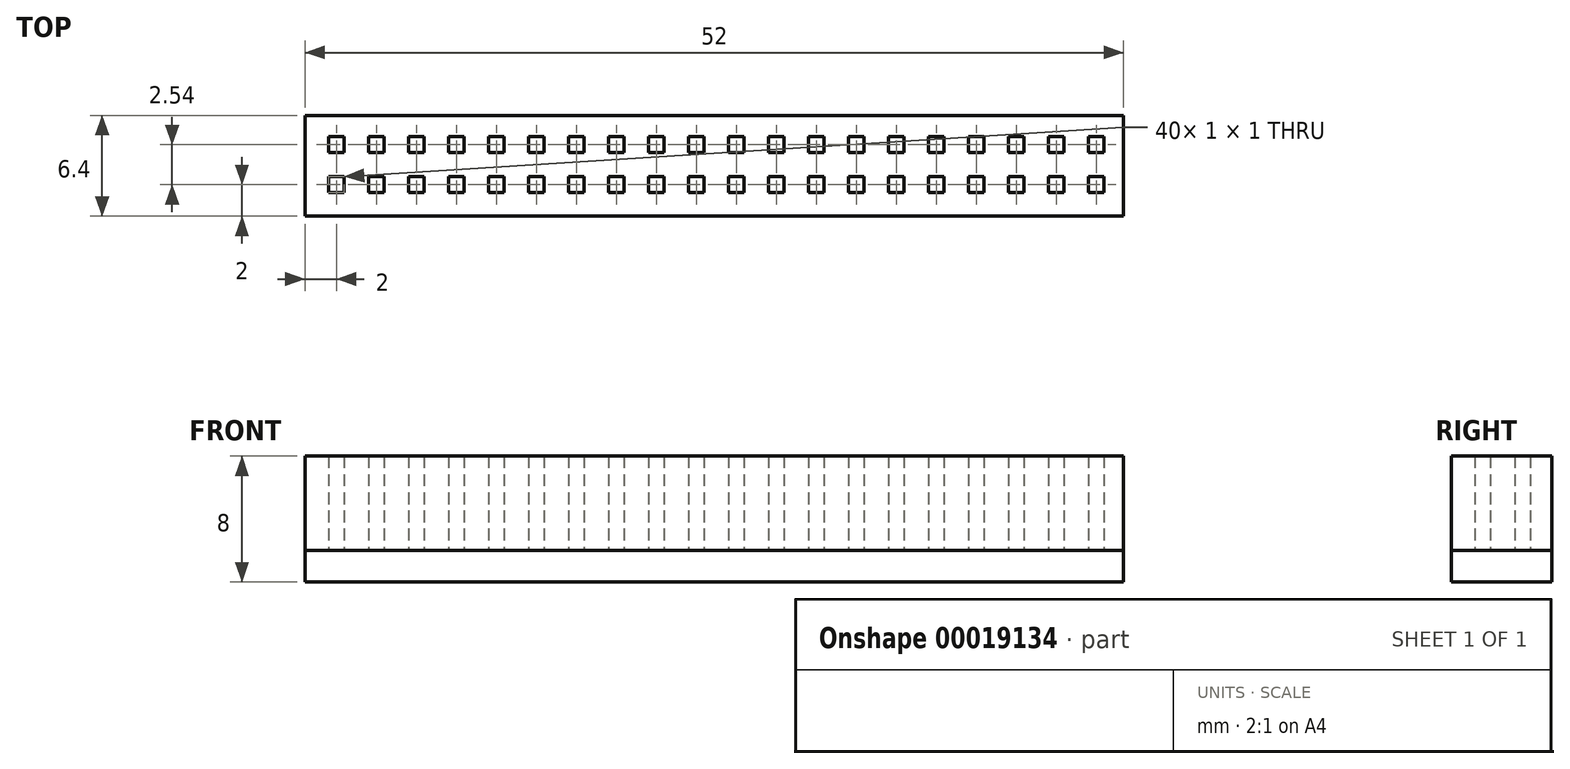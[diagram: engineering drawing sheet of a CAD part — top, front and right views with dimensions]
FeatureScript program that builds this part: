
annotation { "Feature Type Name" : "Feature", "Feature Type Description" : "" }
export const myFeature = defineFeature(function(context is Context, id is Id, definition is map)
    precondition{}
    {
        {
            var Q0;
            Q0=qCreatedBy(makeId("Top.planeOp"),FACE);
            var sketch = newSketch(context, id + "F0", { "sketchPlane" : qUnion([Q0])});
            skLineSegment(sketch, "E0.bottom", {"start": v(0, 0) * mm, "end": v(52, 0) * mm});
            skLineSegment(sketch, "E0.top", {"start": v(0, 6.4) * mm, "end": v(52, 6.4) * mm});
            skLineSegment(sketch, "E0.left", {"start": v(0, 0) * mm, "end": v(0, 6.4) * mm});
            skLineSegment(sketch, "E0.right", {"start": v(52, 0) * mm, "end": v(52, 6.4) * mm});
            skLineSegment(sketch, "E1.bottom", {"start": v(1.5, 1.5) * mm, "end": v(2.5, 1.5) * mm});
            skLineSegment(sketch, "E1.top", {"start": v(1.5, 2.5) * mm, "end": v(2.5, 2.5) * mm});
            skLineSegment(sketch, "E1.left", {"start": v(1.5, 1.5) * mm, "end": v(1.5, 2.5) * mm});
            skLineSegment(sketch, "E1.right", {"start": v(2.5, 1.5) * mm, "end": v(2.5, 2.5) * mm});
            skLineSegment(sketch, "E2.0.1.0", {"start": v(2.5, 4.04) * mm, "end": v(2.5, 5.04) * mm});
            skLineSegment(sketch, "E2.0.1.1", {"start": v(1.5, 4.04) * mm, "end": v(1.5, 5.04) * mm});
            skLineSegment(sketch, "E2.0.1.2", {"start": v(1.5, 5.04) * mm, "end": v(2.5, 5.04) * mm});
            skLineSegment(sketch, "E2.0.1.3", {"start": v(1.5, 4.04) * mm, "end": v(2.5, 4.04) * mm});
            skLineSegment(sketch, "E2.1.0.0", {"start": v(5.04, 1.5) * mm, "end": v(5.04, 2.5) * mm});
            skLineSegment(sketch, "E2.1.0.1", {"start": v(4.04, 1.5) * mm, "end": v(4.04, 2.5) * mm});
            skLineSegment(sketch, "E2.1.0.2", {"start": v(4.04, 2.5) * mm, "end": v(5.04, 2.5) * mm});
            skLineSegment(sketch, "E2.1.0.3", {"start": v(4.04, 1.5) * mm, "end": v(5.04, 1.5) * mm});
            skLineSegment(sketch, "E2.1.1.0", {"start": v(5.04, 4.04) * mm, "end": v(5.04, 5.04) * mm});
            skLineSegment(sketch, "E2.1.1.1", {"start": v(4.04, 4.04) * mm, "end": v(4.04, 5.04) * mm});
            skLineSegment(sketch, "E2.1.1.2", {"start": v(4.04, 5.04) * mm, "end": v(5.04, 5.04) * mm});
            skLineSegment(sketch, "E2.1.1.3", {"start": v(4.04, 4.04) * mm, "end": v(5.04, 4.04) * mm});
            skLineSegment(sketch, "E2.2.0.0", {"start": v(7.58, 1.5) * mm, "end": v(7.58, 2.5) * mm});
            skLineSegment(sketch, "E2.2.0.1", {"start": v(6.58, 1.5) * mm, "end": v(6.58, 2.5) * mm});
            skLineSegment(sketch, "E2.2.0.2", {"start": v(6.58, 2.5) * mm, "end": v(7.58, 2.5) * mm});
            skLineSegment(sketch, "E2.2.0.3", {"start": v(6.58, 1.5) * mm, "end": v(7.58, 1.5) * mm});
            skLineSegment(sketch, "E2.2.1.0", {"start": v(7.58, 4.04) * mm, "end": v(7.58, 5.04) * mm});
            skLineSegment(sketch, "E2.2.1.1", {"start": v(6.58, 4.04) * mm, "end": v(6.58, 5.04) * mm});
            skLineSegment(sketch, "E2.2.1.2", {"start": v(6.58, 5.04) * mm, "end": v(7.58, 5.04) * mm});
            skLineSegment(sketch, "E2.2.1.3", {"start": v(6.58, 4.04) * mm, "end": v(7.58, 4.04) * mm});
            skLineSegment(sketch, "E2.3.0.0", {"start": v(10.12, 1.5) * mm, "end": v(10.12, 2.5) * mm});
            skLineSegment(sketch, "E2.3.0.1", {"start": v(9.12, 1.5) * mm, "end": v(9.12, 2.5) * mm});
            skLineSegment(sketch, "E2.3.0.2", {"start": v(9.12, 2.5) * mm, "end": v(10.12, 2.5) * mm});
            skLineSegment(sketch, "E2.3.0.3", {"start": v(9.12, 1.5) * mm, "end": v(10.12, 1.5) * mm});
            skLineSegment(sketch, "E2.3.1.0", {"start": v(10.12, 4.04) * mm, "end": v(10.12, 5.04) * mm});
            skLineSegment(sketch, "E2.3.1.1", {"start": v(9.12, 4.04) * mm, "end": v(9.12, 5.04) * mm});
            skLineSegment(sketch, "E2.3.1.2", {"start": v(9.12, 5.04) * mm, "end": v(10.12, 5.04) * mm});
            skLineSegment(sketch, "E2.3.1.3", {"start": v(9.12, 4.04) * mm, "end": v(10.12, 4.04) * mm});
            skLineSegment(sketch, "E2.4.0.0", {"start": v(12.66, 1.5) * mm, "end": v(12.66, 2.5) * mm});
            skLineSegment(sketch, "E2.4.0.1", {"start": v(11.66, 1.5) * mm, "end": v(11.66, 2.5) * mm});
            skLineSegment(sketch, "E2.4.0.2", {"start": v(11.66, 2.5) * mm, "end": v(12.66, 2.5) * mm});
            skLineSegment(sketch, "E2.4.0.3", {"start": v(11.66, 1.5) * mm, "end": v(12.66, 1.5) * mm});
            skLineSegment(sketch, "E2.4.1.0", {"start": v(12.66, 4.04) * mm, "end": v(12.66, 5.04) * mm});
            skLineSegment(sketch, "E2.4.1.1", {"start": v(11.66, 4.04) * mm, "end": v(11.66, 5.04) * mm});
            skLineSegment(sketch, "E2.4.1.2", {"start": v(11.66, 5.04) * mm, "end": v(12.66, 5.04) * mm});
            skLineSegment(sketch, "E2.4.1.3", {"start": v(11.66, 4.04) * mm, "end": v(12.66, 4.04) * mm});
            skLineSegment(sketch, "E2.5.0.0", {"start": v(15.2, 1.5) * mm, "end": v(15.2, 2.5) * mm});
            skLineSegment(sketch, "E2.5.0.1", {"start": v(14.2, 1.5) * mm, "end": v(14.2, 2.5) * mm});
            skLineSegment(sketch, "E2.5.0.2", {"start": v(14.2, 2.5) * mm, "end": v(15.2, 2.5) * mm});
            skLineSegment(sketch, "E2.5.0.3", {"start": v(14.2, 1.5) * mm, "end": v(15.2, 1.5) * mm});
            skLineSegment(sketch, "E2.5.1.0", {"start": v(15.2, 4.04) * mm, "end": v(15.2, 5.04) * mm});
            skLineSegment(sketch, "E2.5.1.1", {"start": v(14.2, 4.04) * mm, "end": v(14.2, 5.04) * mm});
            skLineSegment(sketch, "E2.5.1.2", {"start": v(14.2, 5.04) * mm, "end": v(15.2, 5.04) * mm});
            skLineSegment(sketch, "E2.5.1.3", {"start": v(14.2, 4.04) * mm, "end": v(15.2, 4.04) * mm});
            skLineSegment(sketch, "E2.6.0.0", {"start": v(17.74, 1.5) * mm, "end": v(17.74, 2.5) * mm});
            skLineSegment(sketch, "E2.6.0.1", {"start": v(16.74, 1.5) * mm, "end": v(16.74, 2.5) * mm});
            skLineSegment(sketch, "E2.6.0.2", {"start": v(16.74, 2.5) * mm, "end": v(17.74, 2.5) * mm});
            skLineSegment(sketch, "E2.6.0.3", {"start": v(16.74, 1.5) * mm, "end": v(17.74, 1.5) * mm});
            skLineSegment(sketch, "E2.6.1.0", {"start": v(17.74, 4.04) * mm, "end": v(17.74, 5.04) * mm});
            skLineSegment(sketch, "E2.6.1.1", {"start": v(16.74, 4.04) * mm, "end": v(16.74, 5.04) * mm});
            skLineSegment(sketch, "E2.6.1.2", {"start": v(16.74, 5.04) * mm, "end": v(17.74, 5.04) * mm});
            skLineSegment(sketch, "E2.6.1.3", {"start": v(16.74, 4.04) * mm, "end": v(17.74, 4.04) * mm});
            skLineSegment(sketch, "E2.7.0.0", {"start": v(20.28, 1.5) * mm, "end": v(20.28, 2.5) * mm});
            skLineSegment(sketch, "E2.7.0.1", {"start": v(19.28, 1.5) * mm, "end": v(19.28, 2.5) * mm});
            skLineSegment(sketch, "E2.7.0.2", {"start": v(19.28, 2.5) * mm, "end": v(20.28, 2.5) * mm});
            skLineSegment(sketch, "E2.7.0.3", {"start": v(19.28, 1.5) * mm, "end": v(20.28, 1.5) * mm});
            skLineSegment(sketch, "E2.7.1.0", {"start": v(20.28, 4.04) * mm, "end": v(20.28, 5.04) * mm});
            skLineSegment(sketch, "E2.7.1.1", {"start": v(19.28, 4.04) * mm, "end": v(19.28, 5.04) * mm});
            skLineSegment(sketch, "E2.7.1.2", {"start": v(19.28, 5.04) * mm, "end": v(20.28, 5.04) * mm});
            skLineSegment(sketch, "E2.7.1.3", {"start": v(19.28, 4.04) * mm, "end": v(20.28, 4.04) * mm});
            skLineSegment(sketch, "E2.8.0.0", {"start": v(22.82, 1.5) * mm, "end": v(22.82, 2.5) * mm});
            skLineSegment(sketch, "E2.8.0.1", {"start": v(21.82, 1.5) * mm, "end": v(21.82, 2.5) * mm});
            skLineSegment(sketch, "E2.8.0.2", {"start": v(21.82, 2.5) * mm, "end": v(22.82, 2.5) * mm});
            skLineSegment(sketch, "E2.8.0.3", {"start": v(21.82, 1.5) * mm, "end": v(22.82, 1.5) * mm});
            skLineSegment(sketch, "E2.8.1.0", {"start": v(22.82, 4.04) * mm, "end": v(22.82, 5.04) * mm});
            skLineSegment(sketch, "E2.8.1.1", {"start": v(21.82, 4.04) * mm, "end": v(21.82, 5.04) * mm});
            skLineSegment(sketch, "E2.8.1.2", {"start": v(21.82, 5.04) * mm, "end": v(22.82, 5.04) * mm});
            skLineSegment(sketch, "E2.8.1.3", {"start": v(21.82, 4.04) * mm, "end": v(22.82, 4.04) * mm});
            skLineSegment(sketch, "E2.9.0.0", {"start": v(25.36, 1.5) * mm, "end": v(25.36, 2.5) * mm});
            skLineSegment(sketch, "E2.9.0.1", {"start": v(24.36, 1.5) * mm, "end": v(24.36, 2.5) * mm});
            skLineSegment(sketch, "E2.9.0.2", {"start": v(24.36, 2.5) * mm, "end": v(25.36, 2.5) * mm});
            skLineSegment(sketch, "E2.9.0.3", {"start": v(24.36, 1.5) * mm, "end": v(25.36, 1.5) * mm});
            skLineSegment(sketch, "E2.9.1.0", {"start": v(25.36, 4.04) * mm, "end": v(25.36, 5.04) * mm});
            skLineSegment(sketch, "E2.9.1.1", {"start": v(24.36, 4.04) * mm, "end": v(24.36, 5.04) * mm});
            skLineSegment(sketch, "E2.9.1.2", {"start": v(24.36, 5.04) * mm, "end": v(25.36, 5.04) * mm});
            skLineSegment(sketch, "E2.9.1.3", {"start": v(24.36, 4.04) * mm, "end": v(25.36, 4.04) * mm});
            skLineSegment(sketch, "E2.10.0.0", {"start": v(27.9, 1.5) * mm, "end": v(27.9, 2.5) * mm});
            skLineSegment(sketch, "E2.10.0.1", {"start": v(26.9, 1.5) * mm, "end": v(26.9, 2.5) * mm});
            skLineSegment(sketch, "E2.10.0.2", {"start": v(26.9, 2.5) * mm, "end": v(27.9, 2.5) * mm});
            skLineSegment(sketch, "E2.10.0.3", {"start": v(26.9, 1.5) * mm, "end": v(27.9, 1.5) * mm});
            skLineSegment(sketch, "E2.10.1.0", {"start": v(27.9, 4.04) * mm, "end": v(27.9, 5.04) * mm});
            skLineSegment(sketch, "E2.10.1.1", {"start": v(26.9, 4.04) * mm, "end": v(26.9, 5.04) * mm});
            skLineSegment(sketch, "E2.10.1.2", {"start": v(26.9, 5.04) * mm, "end": v(27.9, 5.04) * mm});
            skLineSegment(sketch, "E2.10.1.3", {"start": v(26.9, 4.04) * mm, "end": v(27.9, 4.04) * mm});
            skLineSegment(sketch, "E2.11.0.0", {"start": v(30.44, 1.5) * mm, "end": v(30.44, 2.5) * mm});
            skLineSegment(sketch, "E2.11.0.1", {"start": v(29.44, 1.5) * mm, "end": v(29.44, 2.5) * mm});
            skLineSegment(sketch, "E2.11.0.2", {"start": v(29.44, 2.5) * mm, "end": v(30.44, 2.5) * mm});
            skLineSegment(sketch, "E2.11.0.3", {"start": v(29.44, 1.5) * mm, "end": v(30.44, 1.5) * mm});
            skLineSegment(sketch, "E2.11.1.0", {"start": v(30.44, 4.04) * mm, "end": v(30.44, 5.04) * mm});
            skLineSegment(sketch, "E2.11.1.1", {"start": v(29.44, 4.04) * mm, "end": v(29.44, 5.04) * mm});
            skLineSegment(sketch, "E2.11.1.2", {"start": v(29.44, 5.04) * mm, "end": v(30.44, 5.04) * mm});
            skLineSegment(sketch, "E2.11.1.3", {"start": v(29.44, 4.04) * mm, "end": v(30.44, 4.04) * mm});
            skLineSegment(sketch, "E2.12.0.0", {"start": v(32.98, 1.5) * mm, "end": v(32.98, 2.5) * mm});
            skLineSegment(sketch, "E2.12.0.1", {"start": v(31.98, 1.5) * mm, "end": v(31.98, 2.5) * mm});
            skLineSegment(sketch, "E2.12.0.2", {"start": v(31.98, 2.5) * mm, "end": v(32.98, 2.5) * mm});
            skLineSegment(sketch, "E2.12.0.3", {"start": v(31.98, 1.5) * mm, "end": v(32.98, 1.5) * mm});
            skLineSegment(sketch, "E2.12.1.0", {"start": v(32.98, 4.04) * mm, "end": v(32.98, 5.04) * mm});
            skLineSegment(sketch, "E2.12.1.1", {"start": v(31.98, 4.04) * mm, "end": v(31.98, 5.04) * mm});
            skLineSegment(sketch, "E2.12.1.2", {"start": v(31.98, 5.04) * mm, "end": v(32.98, 5.04) * mm});
            skLineSegment(sketch, "E2.12.1.3", {"start": v(31.98, 4.04) * mm, "end": v(32.98, 4.04) * mm});
            skLineSegment(sketch, "E2.13.0.0", {"start": v(35.52, 1.5) * mm, "end": v(35.52, 2.5) * mm});
            skLineSegment(sketch, "E2.13.0.1", {"start": v(34.52, 1.5) * mm, "end": v(34.52, 2.5) * mm});
            skLineSegment(sketch, "E2.13.0.2", {"start": v(34.52, 2.5) * mm, "end": v(35.52, 2.5) * mm});
            skLineSegment(sketch, "E2.13.0.3", {"start": v(34.52, 1.5) * mm, "end": v(35.52, 1.5) * mm});
            skLineSegment(sketch, "E2.13.1.0", {"start": v(35.52, 4.04) * mm, "end": v(35.52, 5.04) * mm});
            skLineSegment(sketch, "E2.13.1.1", {"start": v(34.52, 4.04) * mm, "end": v(34.52, 5.04) * mm});
            skLineSegment(sketch, "E2.13.1.2", {"start": v(34.52, 5.04) * mm, "end": v(35.52, 5.04) * mm});
            skLineSegment(sketch, "E2.13.1.3", {"start": v(34.52, 4.04) * mm, "end": v(35.52, 4.04) * mm});
            skLineSegment(sketch, "E2.14.0.0", {"start": v(38.06, 1.5) * mm, "end": v(38.06, 2.5) * mm});
            skLineSegment(sketch, "E2.14.0.1", {"start": v(37.06, 1.5) * mm, "end": v(37.06, 2.5) * mm});
            skLineSegment(sketch, "E2.14.0.2", {"start": v(37.06, 2.5) * mm, "end": v(38.06, 2.5) * mm});
            skLineSegment(sketch, "E2.14.0.3", {"start": v(37.06, 1.5) * mm, "end": v(38.06, 1.5) * mm});
            skLineSegment(sketch, "E2.14.1.0", {"start": v(38.06, 4.04) * mm, "end": v(38.06, 5.04) * mm});
            skLineSegment(sketch, "E2.14.1.1", {"start": v(37.06, 4.04) * mm, "end": v(37.06, 5.04) * mm});
            skLineSegment(sketch, "E2.14.1.2", {"start": v(37.06, 5.04) * mm, "end": v(38.06, 5.04) * mm});
            skLineSegment(sketch, "E2.14.1.3", {"start": v(37.06, 4.04) * mm, "end": v(38.06, 4.04) * mm});
            skLineSegment(sketch, "E2.15.0.0", {"start": v(40.6, 1.5) * mm, "end": v(40.6, 2.5) * mm});
            skLineSegment(sketch, "E2.15.0.1", {"start": v(39.6, 1.5) * mm, "end": v(39.6, 2.5) * mm});
            skLineSegment(sketch, "E2.15.0.2", {"start": v(39.6, 2.5) * mm, "end": v(40.6, 2.5) * mm});
            skLineSegment(sketch, "E2.15.0.3", {"start": v(39.6, 1.5) * mm, "end": v(40.6, 1.5) * mm});
            skLineSegment(sketch, "E2.15.1.0", {"start": v(40.6, 4.04) * mm, "end": v(40.6, 5.04) * mm});
            skLineSegment(sketch, "E2.15.1.1", {"start": v(39.6, 4.04) * mm, "end": v(39.6, 5.04) * mm});
            skLineSegment(sketch, "E2.15.1.2", {"start": v(39.6, 5.04) * mm, "end": v(40.6, 5.04) * mm});
            skLineSegment(sketch, "E2.15.1.3", {"start": v(39.6, 4.04) * mm, "end": v(40.6, 4.04) * mm});
            skLineSegment(sketch, "E2.16.0.0", {"start": v(43.14, 1.5) * mm, "end": v(43.14, 2.5) * mm});
            skLineSegment(sketch, "E2.16.0.1", {"start": v(42.14, 1.5) * mm, "end": v(42.14, 2.5) * mm});
            skLineSegment(sketch, "E2.16.0.2", {"start": v(42.14, 2.5) * mm, "end": v(43.14, 2.5) * mm});
            skLineSegment(sketch, "E2.16.0.3", {"start": v(42.14, 1.5) * mm, "end": v(43.14, 1.5) * mm});
            skLineSegment(sketch, "E2.16.1.0", {"start": v(43.14, 4.04) * mm, "end": v(43.14, 5.04) * mm});
            skLineSegment(sketch, "E2.16.1.1", {"start": v(42.14, 4.04) * mm, "end": v(42.14, 5.04) * mm});
            skLineSegment(sketch, "E2.16.1.2", {"start": v(42.14, 5.04) * mm, "end": v(43.14, 5.04) * mm});
            skLineSegment(sketch, "E2.16.1.3", {"start": v(42.14, 4.04) * mm, "end": v(43.14, 4.04) * mm});
            skLineSegment(sketch, "E2.17.0.0", {"start": v(45.68, 1.5) * mm, "end": v(45.68, 2.5) * mm});
            skLineSegment(sketch, "E2.17.0.1", {"start": v(44.68, 1.5) * mm, "end": v(44.68, 2.5) * mm});
            skLineSegment(sketch, "E2.17.0.2", {"start": v(44.68, 2.5) * mm, "end": v(45.68, 2.5) * mm});
            skLineSegment(sketch, "E2.17.0.3", {"start": v(44.68, 1.5) * mm, "end": v(45.68, 1.5) * mm});
            skLineSegment(sketch, "E2.17.1.0", {"start": v(45.68, 4.04) * mm, "end": v(45.68, 5.04) * mm});
            skLineSegment(sketch, "E2.17.1.1", {"start": v(44.68, 4.04) * mm, "end": v(44.68, 5.04) * mm});
            skLineSegment(sketch, "E2.17.1.2", {"start": v(44.68, 5.04) * mm, "end": v(45.68, 5.04) * mm});
            skLineSegment(sketch, "E2.17.1.3", {"start": v(44.68, 4.04) * mm, "end": v(45.68, 4.04) * mm});
            skLineSegment(sketch, "E2.18.0.0", {"start": v(48.22, 1.5) * mm, "end": v(48.22, 2.5) * mm});
            skLineSegment(sketch, "E2.18.0.1", {"start": v(47.22, 1.5) * mm, "end": v(47.22, 2.5) * mm});
            skLineSegment(sketch, "E2.18.0.2", {"start": v(47.22, 2.5) * mm, "end": v(48.22, 2.5) * mm});
            skLineSegment(sketch, "E2.18.0.3", {"start": v(47.22, 1.5) * mm, "end": v(48.22, 1.5) * mm});
            skLineSegment(sketch, "E2.18.1.0", {"start": v(48.22, 4.04) * mm, "end": v(48.22, 5.04) * mm});
            skLineSegment(sketch, "E2.18.1.1", {"start": v(47.22, 4.04) * mm, "end": v(47.22, 5.04) * mm});
            skLineSegment(sketch, "E2.18.1.2", {"start": v(47.22, 5.04) * mm, "end": v(48.22, 5.04) * mm});
            skLineSegment(sketch, "E2.18.1.3", {"start": v(47.22, 4.04) * mm, "end": v(48.22, 4.04) * mm});
            skLineSegment(sketch, "E2.19.0.0", {"start": v(50.76, 1.5) * mm, "end": v(50.76, 2.5) * mm});
            skLineSegment(sketch, "E2.19.0.1", {"start": v(49.76, 1.5) * mm, "end": v(49.76, 2.5) * mm});
            skLineSegment(sketch, "E2.19.0.2", {"start": v(49.76, 2.5) * mm, "end": v(50.76, 2.5) * mm});
            skLineSegment(sketch, "E2.19.0.3", {"start": v(49.76, 1.5) * mm, "end": v(50.76, 1.5) * mm});
            skLineSegment(sketch, "E2.19.1.0", {"start": v(50.76, 4.04) * mm, "end": v(50.76, 5.04) * mm});
            skLineSegment(sketch, "E2.19.1.1", {"start": v(49.76, 4.04) * mm, "end": v(49.76, 5.04) * mm});
            skLineSegment(sketch, "E2.19.1.2", {"start": v(49.76, 5.04) * mm, "end": v(50.76, 5.04) * mm});
            skLineSegment(sketch, "E2.19.1.3", {"start": v(49.76, 4.04) * mm, "end": v(50.76, 4.04) * mm});
            skLineSegment(sketch, "E2.direction1", {"start": v(2.5, 1.5) * mm, "end": v(5.04, 1.5) * mm, "construction": true});
            skLineSegment(sketch, "E2.direction2", {"start": v(2.5, 1.5) * mm, "end": v(2.5, 4.04) * mm, "construction": true});
            skSolve(sketch);
        }
        {
            var Q0;
            Q0=makeQuery(id+"F0.imprint","IMPRINT",FACE,{"disambiguationData":[TD([[makeQuery(id+"F0.imprint","IMPRINT",EDGE,{"derivedFrom":sQuery(id+"F0.wireOp",EDGE,"E0.bottom")}),1.0]])]});
            extrude(context, id + "F1", {"entities" : qUnion([Q0]), "depth" : 6 * mm});
        }
        {
            var Q0;
            Q0=makeQuery(id+"F0.imprint","IMPRINT",FACE,{"disambiguationData":[TD([[makeQuery(id+"F0.imprint","IMPRINT",EDGE,{"derivedFrom":sQuery(id+"F0.wireOp",EDGE,"E0.bottom")}),1.0]])]});
            var Q1;
            Q1=makeQuery(id+"F0.imprint","IMPRINT",FACE,{"disambiguationData":[TD([[makeQuery(id+"F0.imprint","IMPRINT",EDGE,{"derivedFrom":sQuery(id+"F0.wireOp",EDGE,"E1.bottom")}),1.0]])]});
            var Q2;
            Q2=makeQuery(id+"F0.imprint","IMPRINT",FACE,{"disambiguationData":[TD([[makeQuery(id+"F0.imprint","IMPRINT",EDGE,{"derivedFrom":sQuery(id+"F0.wireOp",EDGE,"E2.0.1.0")}),1.0]])]});
            var Q3;
            Q3=makeQuery(id+"F0.imprint","IMPRINT",FACE,{"disambiguationData":[TD([[makeQuery(id+"F0.imprint","IMPRINT",EDGE,{"derivedFrom":sQuery(id+"F0.wireOp",EDGE,"E2.1.1.0")}),1.0]])]});
            var Q4;
            Q4=makeQuery(id+"F0.imprint","IMPRINT",FACE,{"disambiguationData":[TD([[makeQuery(id+"F0.imprint","IMPRINT",EDGE,{"derivedFrom":sQuery(id+"F0.wireOp",EDGE,"E2.1.0.0")}),1.0]])]});
            var Q5;
            Q5=makeQuery(id+"F0.imprint","IMPRINT",FACE,{"disambiguationData":[TD([[makeQuery(id+"F0.imprint","IMPRINT",EDGE,{"derivedFrom":sQuery(id+"F0.wireOp",EDGE,"E2.2.0.0")}),1.0]])]});
            var Q6;
            Q6=makeQuery(id+"F0.imprint","IMPRINT",FACE,{"disambiguationData":[TD([[makeQuery(id+"F0.imprint","IMPRINT",EDGE,{"derivedFrom":sQuery(id+"F0.wireOp",EDGE,"E2.2.1.0")}),1.0]])]});
            var Q7;
            Q7=makeQuery(id+"F0.imprint","IMPRINT",FACE,{"disambiguationData":[TD([[makeQuery(id+"F0.imprint","IMPRINT",EDGE,{"derivedFrom":sQuery(id+"F0.wireOp",EDGE,"E2.3.1.0")}),1.0]])]});
            var Q8;
            Q8=makeQuery(id+"F0.imprint","IMPRINT",FACE,{"disambiguationData":[TD([[makeQuery(id+"F0.imprint","IMPRINT",EDGE,{"derivedFrom":sQuery(id+"F0.wireOp",EDGE,"E2.3.0.0")}),1.0]])]});
            var Q9;
            Q9=makeQuery(id+"F0.imprint","IMPRINT",FACE,{"disambiguationData":[TD([[makeQuery(id+"F0.imprint","IMPRINT",EDGE,{"derivedFrom":sQuery(id+"F0.wireOp",EDGE,"E2.4.0.0")}),1.0]])]});
            var Q10;
            Q10=makeQuery(id+"F0.imprint","IMPRINT",FACE,{"disambiguationData":[TD([[makeQuery(id+"F0.imprint","IMPRINT",EDGE,{"derivedFrom":sQuery(id+"F0.wireOp",EDGE,"E2.4.1.0")}),1.0]])]});
            var Q11;
            Q11=makeQuery(id+"F0.imprint","IMPRINT",FACE,{"disambiguationData":[TD([[makeQuery(id+"F0.imprint","IMPRINT",EDGE,{"derivedFrom":sQuery(id+"F0.wireOp",EDGE,"E2.5.1.0")}),1.0]])]});
            var Q12;
            Q12=makeQuery(id+"F0.imprint","IMPRINT",FACE,{"disambiguationData":[TD([[makeQuery(id+"F0.imprint","IMPRINT",EDGE,{"derivedFrom":sQuery(id+"F0.wireOp",EDGE,"E2.5.0.0")}),1.0]])]});
            var Q13;
            Q13=makeQuery(id+"F0.imprint","IMPRINT",FACE,{"disambiguationData":[TD([[makeQuery(id+"F0.imprint","IMPRINT",EDGE,{"derivedFrom":sQuery(id+"F0.wireOp",EDGE,"E2.6.0.0")}),1.0]])]});
            var Q14;
            Q14=makeQuery(id+"F0.imprint","IMPRINT",FACE,{"disambiguationData":[TD([[makeQuery(id+"F0.imprint","IMPRINT",EDGE,{"derivedFrom":sQuery(id+"F0.wireOp",EDGE,"E2.6.1.0")}),1.0]])]});
            var Q15;
            Q15=makeQuery(id+"F0.imprint","IMPRINT",FACE,{"disambiguationData":[TD([[makeQuery(id+"F0.imprint","IMPRINT",EDGE,{"derivedFrom":sQuery(id+"F0.wireOp",EDGE,"E2.7.1.0")}),1.0]])]});
            var Q16;
            Q16=makeQuery(id+"F0.imprint","IMPRINT",FACE,{"disambiguationData":[TD([[makeQuery(id+"F0.imprint","IMPRINT",EDGE,{"derivedFrom":sQuery(id+"F0.wireOp",EDGE,"E2.7.0.0")}),1.0]])]});
            var Q17;
            Q17=makeQuery(id+"F0.imprint","IMPRINT",FACE,{"disambiguationData":[TD([[makeQuery(id+"F0.imprint","IMPRINT",EDGE,{"derivedFrom":sQuery(id+"F0.wireOp",EDGE,"E2.8.0.0")}),1.0]])]});
            var Q18;
            Q18=makeQuery(id+"F0.imprint","IMPRINT",FACE,{"disambiguationData":[TD([[makeQuery(id+"F0.imprint","IMPRINT",EDGE,{"derivedFrom":sQuery(id+"F0.wireOp",EDGE,"E2.8.1.0")}),1.0]])]});
            var Q19;
            Q19=makeQuery(id+"F0.imprint","IMPRINT",FACE,{"disambiguationData":[TD([[makeQuery(id+"F0.imprint","IMPRINT",EDGE,{"derivedFrom":sQuery(id+"F0.wireOp",EDGE,"E2.9.1.0")}),1.0]])]});
            var Q20;
            Q20=makeQuery(id+"F0.imprint","IMPRINT",FACE,{"disambiguationData":[TD([[makeQuery(id+"F0.imprint","IMPRINT",EDGE,{"derivedFrom":sQuery(id+"F0.wireOp",EDGE,"E2.9.0.0")}),1.0]])]});
            var Q21;
            Q21=makeQuery(id+"F0.imprint","IMPRINT",FACE,{"disambiguationData":[TD([[makeQuery(id+"F0.imprint","IMPRINT",EDGE,{"derivedFrom":sQuery(id+"F0.wireOp",EDGE,"E2.10.0.0")}),1.0]])]});
            var Q22;
            Q22=makeQuery(id+"F0.imprint","IMPRINT",FACE,{"disambiguationData":[TD([[makeQuery(id+"F0.imprint","IMPRINT",EDGE,{"derivedFrom":sQuery(id+"F0.wireOp",EDGE,"E2.10.1.0")}),1.0]])]});
            var Q23;
            Q23=makeQuery(id+"F0.imprint","IMPRINT",FACE,{"disambiguationData":[TD([[makeQuery(id+"F0.imprint","IMPRINT",EDGE,{"derivedFrom":sQuery(id+"F0.wireOp",EDGE,"E2.11.1.0")}),1.0]])]});
            var Q24;
            Q24=makeQuery(id+"F0.imprint","IMPRINT",FACE,{"disambiguationData":[TD([[makeQuery(id+"F0.imprint","IMPRINT",EDGE,{"derivedFrom":sQuery(id+"F0.wireOp",EDGE,"E2.11.0.0")}),1.0]])]});
            var Q25;
            Q25=makeQuery(id+"F0.imprint","IMPRINT",FACE,{"disambiguationData":[TD([[makeQuery(id+"F0.imprint","IMPRINT",EDGE,{"derivedFrom":sQuery(id+"F0.wireOp",EDGE,"E2.12.0.0")}),1.0]])]});
            var Q26;
            Q26=makeQuery(id+"F0.imprint","IMPRINT",FACE,{"disambiguationData":[TD([[makeQuery(id+"F0.imprint","IMPRINT",EDGE,{"derivedFrom":sQuery(id+"F0.wireOp",EDGE,"E2.12.1.0")}),1.0]])]});
            var Q27;
            Q27=makeQuery(id+"F0.imprint","IMPRINT",FACE,{"disambiguationData":[TD([[makeQuery(id+"F0.imprint","IMPRINT",EDGE,{"derivedFrom":sQuery(id+"F0.wireOp",EDGE,"E2.13.1.0")}),1.0]])]});
            var Q28;
            Q28=makeQuery(id+"F0.imprint","IMPRINT",FACE,{"disambiguationData":[TD([[makeQuery(id+"F0.imprint","IMPRINT",EDGE,{"derivedFrom":sQuery(id+"F0.wireOp",EDGE,"E2.13.0.0")}),1.0]])]});
            var Q29;
            Q29=makeQuery(id+"F0.imprint","IMPRINT",FACE,{"disambiguationData":[TD([[makeQuery(id+"F0.imprint","IMPRINT",EDGE,{"derivedFrom":sQuery(id+"F0.wireOp",EDGE,"E2.14.0.0")}),1.0]])]});
            var Q30;
            Q30=makeQuery(id+"F0.imprint","IMPRINT",FACE,{"disambiguationData":[TD([[makeQuery(id+"F0.imprint","IMPRINT",EDGE,{"derivedFrom":sQuery(id+"F0.wireOp",EDGE,"E2.14.1.0")}),1.0]])]});
            var Q31;
            Q31=makeQuery(id+"F0.imprint","IMPRINT",FACE,{"disambiguationData":[TD([[makeQuery(id+"F0.imprint","IMPRINT",EDGE,{"derivedFrom":sQuery(id+"F0.wireOp",EDGE,"E2.15.1.0")}),1.0]])]});
            var Q32;
            Q32=makeQuery(id+"F0.imprint","IMPRINT",FACE,{"disambiguationData":[TD([[makeQuery(id+"F0.imprint","IMPRINT",EDGE,{"derivedFrom":sQuery(id+"F0.wireOp",EDGE,"E2.15.0.0")}),1.0]])]});
            var Q33;
            Q33=makeQuery(id+"F0.imprint","IMPRINT",FACE,{"disambiguationData":[TD([[makeQuery(id+"F0.imprint","IMPRINT",EDGE,{"derivedFrom":sQuery(id+"F0.wireOp",EDGE,"E2.16.0.0")}),1.0]])]});
            var Q34;
            Q34=makeQuery(id+"F0.imprint","IMPRINT",FACE,{"disambiguationData":[TD([[makeQuery(id+"F0.imprint","IMPRINT",EDGE,{"derivedFrom":sQuery(id+"F0.wireOp",EDGE,"E2.16.1.0")}),1.0]])]});
            var Q35;
            Q35=makeQuery(id+"F0.imprint","IMPRINT",FACE,{"disambiguationData":[TD([[makeQuery(id+"F0.imprint","IMPRINT",EDGE,{"derivedFrom":sQuery(id+"F0.wireOp",EDGE,"E2.17.1.0")}),1.0]])]});
            var Q36;
            Q36=makeQuery(id+"F0.imprint","IMPRINT",FACE,{"disambiguationData":[TD([[makeQuery(id+"F0.imprint","IMPRINT",EDGE,{"derivedFrom":sQuery(id+"F0.wireOp",EDGE,"E2.17.0.0")}),1.0]])]});
            var Q37;
            Q37=makeQuery(id+"F0.imprint","IMPRINT",FACE,{"disambiguationData":[TD([[makeQuery(id+"F0.imprint","IMPRINT",EDGE,{"derivedFrom":sQuery(id+"F0.wireOp",EDGE,"E2.18.0.0")}),1.0]])]});
            var Q38;
            Q38=makeQuery(id+"F0.imprint","IMPRINT",FACE,{"disambiguationData":[TD([[makeQuery(id+"F0.imprint","IMPRINT",EDGE,{"derivedFrom":sQuery(id+"F0.wireOp",EDGE,"E2.18.1.0")}),1.0]])]});
            var Q39;
            Q39=makeQuery(id+"F0.imprint","IMPRINT",FACE,{"disambiguationData":[TD([[makeQuery(id+"F0.imprint","IMPRINT",EDGE,{"derivedFrom":sQuery(id+"F0.wireOp",EDGE,"E2.19.1.0")}),1.0]])]});
            var Q40;
            Q40=makeQuery(id+"F0.imprint","IMPRINT",FACE,{"disambiguationData":[TD([[makeQuery(id+"F0.imprint","IMPRINT",EDGE,{"derivedFrom":sQuery(id+"F0.wireOp",EDGE,"E2.19.0.0")}),1.0]])]});
            extrude(context, id + "F2", {"entities" : qUnion([Q0, Q1, Q2, Q3, Q4, Q5, Q6, Q7, Q8, Q9, Q10, Q11, Q12, Q13, Q14, Q15, Q16, Q17, Q18, Q19, Q20, Q21, Q22, Q23, Q24, Q25, Q26, Q27, Q28, Q29, Q30, Q31, Q32, Q33, Q34, Q35, Q36, Q37, Q38, Q39, Q40]), "oppositeDirection" : true, "depth" : 2 * mm});
        }
    });
